# Revit family: 88R0313XX
name_source: partatom
category: Furniture
units: mm (PartAtom-declared; Revit-internal decimal feet)

## family parameters
Always vertical = Yes
Cut with Voids When Loaded = No
Host = Wall
Room Calculation Point = No
Shared = No

## types (2) — shared parameters
Edge Ext-Dist = 0' - 0 7/16"
Manufacturer = Palmer Hamilton
Product = https://palmerhamilton.com
T-Edge-Dist = 0' - 0 1/2"
Type Comments = Wall Pocket
URL = https://palmerhamilton.com
V-CL-1 = Yes

## per-type parameters (varying)
| type | 36W CL | Depth | Description | Double Retro-Fit | H-CL-10"L-1 | Side Ch | Single Retro Fit | V-4.5-1 | V-CL-2 | V-CL-5 | V-CL-7 |
| 88R031312 | No | 0' - 5 7/8" | Single Retro-Fit Pocket | No | No | 0' - 4" | Yes | No | No | Yes | No |
| 88R031324 | Yes | 0' - 11 7/16" | Double Retro-Fit Pocket | Yes | Yes | 0' - 10 1/16" | No | Yes | Yes | No | Yes |

note: column(s) folded — value = type name in every type: Model

## geometry (parser evidence)
native form markers: Sweep x34
no freeform markers — native parametric forms only
